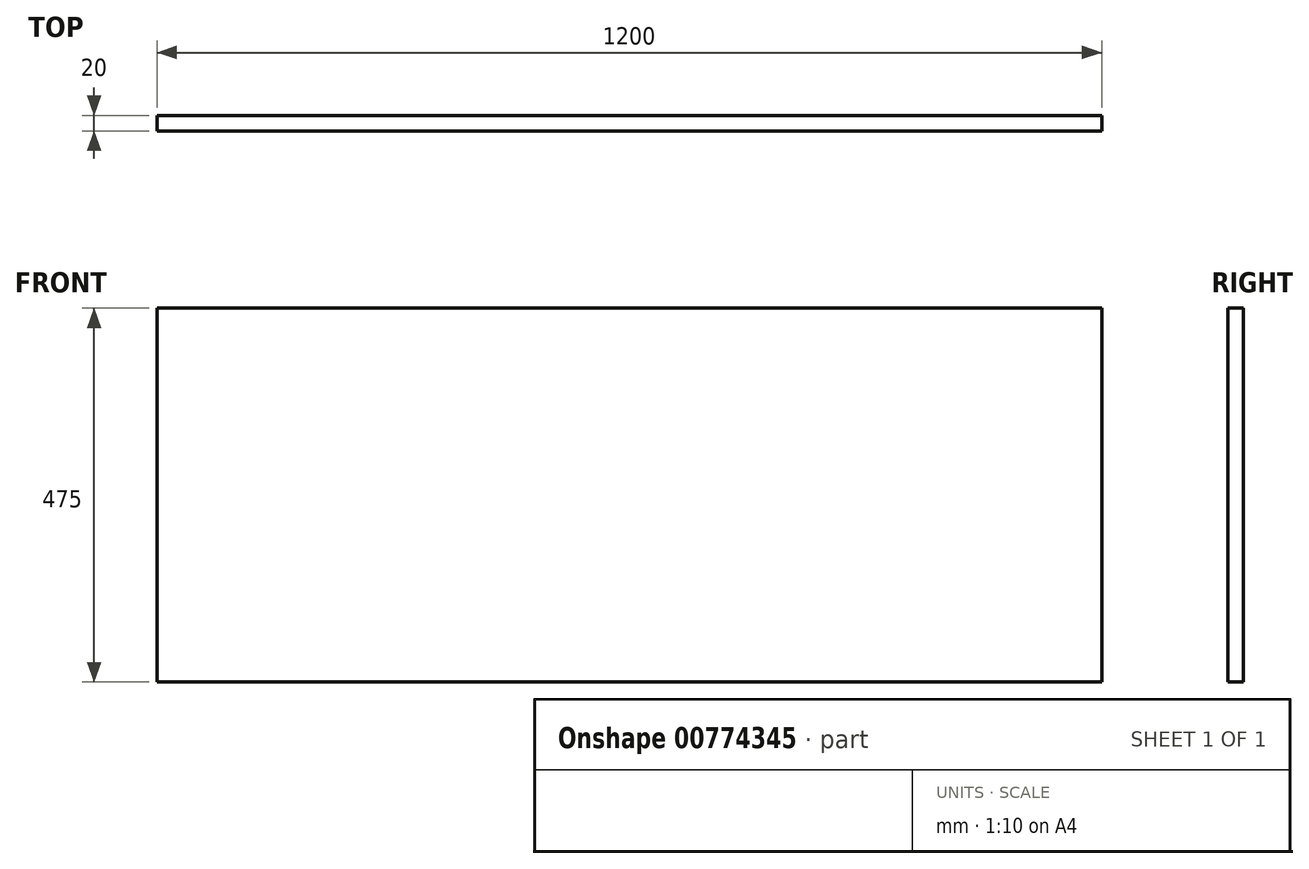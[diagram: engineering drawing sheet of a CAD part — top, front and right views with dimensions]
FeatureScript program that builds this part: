
annotation { "Feature Type Name" : "Feature", "Feature Type Description" : "" }
export const myFeature = defineFeature(function(context is Context, id is Id, definition is map)
    precondition{}
    {
        {
            var Q0;
            Q0=qCreatedBy(makeId("Top.planeOp"),FACE);
            var sketch = newSketch(context, id + "F0", { "sketchPlane" : qUnion([Q0])});
            skLineSegment(sketch, "E0.bottom", {"start": v(0, 0) * mm, "end": v(1200, 0) * mm});
            skLineSegment(sketch, "E0.top", {"start": v(0, 20) * mm, "end": v(1200, 20) * mm});
            skLineSegment(sketch, "E0.left", {"start": v(0, 0) * mm, "end": v(0, 20) * mm});
            skLineSegment(sketch, "E0.right", {"start": v(1200, 0) * mm, "end": v(1200, 20) * mm});
            skSolve(sketch);
        }
        {
            var Q0;
            Q0=makeQuery(id+"F0.imprint","IMPRINT",FACE,{"disambiguationData":[TD([[makeQuery(id+"F0.imprint","IMPRINT",EDGE,{"derivedFrom":sQuery(id+"F0.wireOp",EDGE,"E0.bottom")}),1.0]])]});
            extrude(context, id + "F1", {"entities" : qUnion([Q0]), "depth" : 475 * mm, "offsetDistance" : 25 * mm});
        }
    });
